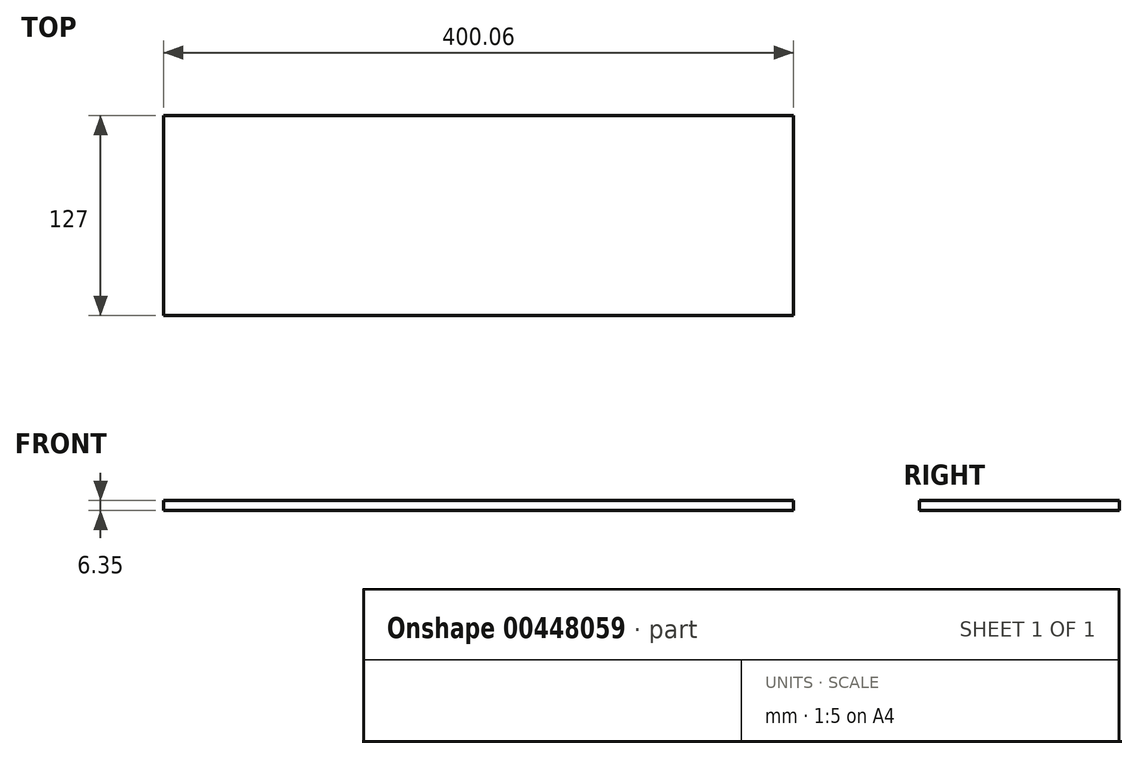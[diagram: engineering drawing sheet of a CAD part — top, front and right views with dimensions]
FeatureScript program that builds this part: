
annotation { "Feature Type Name" : "Feature", "Feature Type Description" : "" }
export const myFeature = defineFeature(function(context is Context, id is Id, definition is map)
    precondition{}
    {
        {
            var Q0;
            Q0=qCreatedBy(makeId("Top.planeOp"),FACE);
            var sketch = newSketch(context, id + "F0", { "sketchPlane" : qUnion([Q0])});
            skLineSegment(sketch, "E0.bottom", {"start": v(-200.03, 63.5) * mm, "end": v(200.03, 63.5) * mm});
            skLineSegment(sketch, "E0.top", {"start": v(-200.03, -63.5) * mm, "end": v(200.03, -63.5) * mm});
            skLineSegment(sketch, "E0.left", {"start": v(-200.03, 63.5) * mm, "end": v(-200.03, -63.5) * mm});
            skLineSegment(sketch, "E0.right", {"start": v(200.03, 63.5) * mm, "end": v(200.03, -63.5) * mm});
            skPoint(sketch, "E0.middle", {"position": v(0, 0) * mm});
            skSolve(sketch);
        }
        {
            var Q0;
            Q0 = qSketchRegion(id + "F0", true);
            extrude(context, id + "F1", {"entities" : qUnion([Q0]), "depth" : 6.35 * mm});
        }
    });
